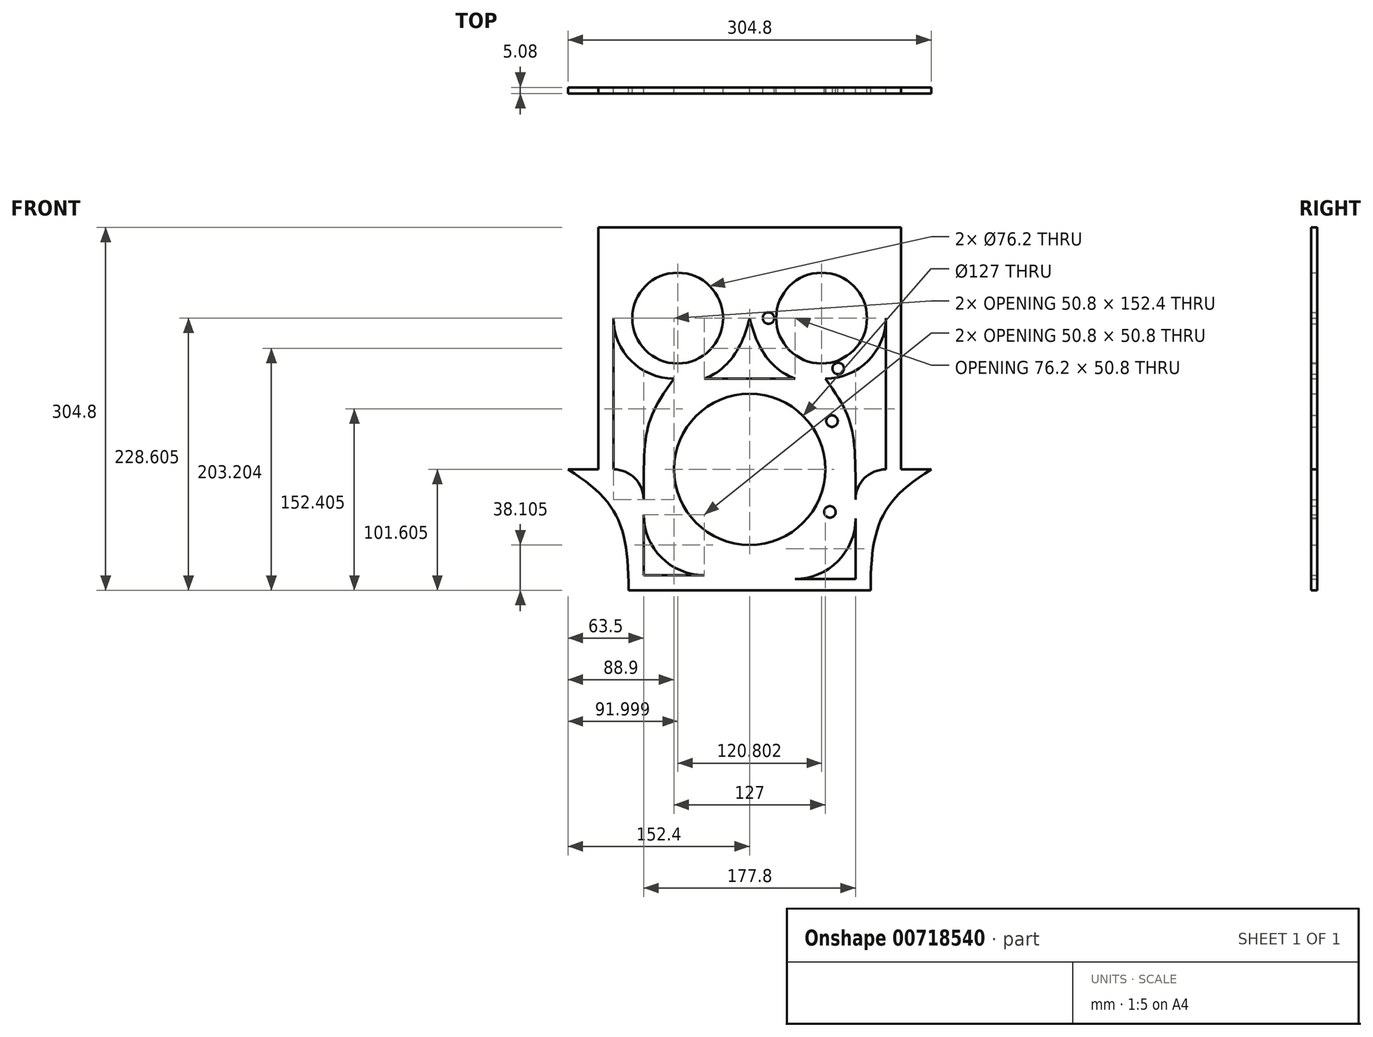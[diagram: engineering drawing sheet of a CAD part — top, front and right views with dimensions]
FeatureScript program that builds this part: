
annotation { "Feature Type Name" : "Feature", "Feature Type Description" : "" }
export const myFeature = defineFeature(function(context is Context, id is Id, definition is map)
    precondition{}
    {
        {
            var Q0;
            Q0=qCreatedBy(makeId("Front.planeOp"),FACE);
            var sketch = newSketch(context, id + "F0", { "sketchPlane" : qUnion([Q0])});
            skCircle(sketch, "E0", {"center": v(-60.4, 86.51) * mm, "radius": 38.1 * mm});
            skCircle(sketch, "E1", {"center": v(15.88, 86.51) * mm, "radius": 38.1 * mm, "construction": true});
            skCircle(sketch, "E2", {"center": v(15.88, 86.51) * mm, "radius": 6.35 * mm, "construction": true});
            skCircle(sketch, "E3", {"center": v(60.4, 86.51) * mm, "radius": 38.1 * mm});
            skLineSegment(sketch, "E4", {"start": v(-60.4, 86.51) * mm, "end": v(60.4, 86.51) * mm, "construction": true});
            skPoint(sketch, "E5", {"position": v(0, 86.51) * mm});
            skLineSegment(sketch, "E6", {"start": v(0, 86.51) * mm, "end": v(0, -40.49) * mm, "construction": true});
            skCircle(sketch, "E7", {"center": v(15.88, 86.51) * mm, "radius": 4.83 * mm});
            skCircle(sketch, "E8", {"center": v(-60.4, 86.51) * mm, "radius": 4.83 * mm});
            skCircle(sketch, "E9", {"center": v(60.4, 86.51) * mm, "radius": 4.83 * mm});
            skLineSegment(sketch, "E10", {"start": v(-60.4, 48.41) * mm, "end": v(-60.4, 23.01) * mm, "construction": true});
            skPoint(sketch, "E11", {"position": v(0, 23.01) * mm});
            skCircle(sketch, "E12", {"center": v(0, -40.49) * mm, "radius": 63.5 * mm});
            skCircle(sketch, "E13", {"center": v(0, -40.49) * mm, "radius": 4.83 * mm});
            skLineSegment(sketch, "E14", {"start": v(0, -40.49) * mm, "end": v(127, -40.49) * mm, "construction": true});
            skLineSegment(sketch, "E15", {"start": v(0, -40.49) * mm, "end": v(-127, -40.49) * mm, "construction": true});
            skLineSegment(sketch, "E16", {"start": v(-127, -40.49) * mm, "end": v(-152.4, -40.49) * mm});
            skLineSegment(sketch, "E17", {"start": v(127, -40.49) * mm, "end": v(152.4, -40.49) * mm});
            skLineSegment(sketch, "E18", {"start": v(0, -40.49) * mm, "end": v(0, -142.09) * mm});
            skLineSegment(sketch, "E19", {"start": v(0, -142.09) * mm, "end": v(101.6, -142.09) * mm});
            skLineSegment(sketch, "E20", {"start": v(0, -142.09) * mm, "end": v(-101.6, -142.09) * mm});
            skFitSpline(sketch, "E21", {"points": [v(152.4, -40.49) * mm, v(101.6, -142.09) * mm], "startDerivative": vector(-128.12, -79.75) * mm, "endDerivative": vector(0, -160.77) * mm});
            skFitSpline(sketch, "E22", {"points": [v(-152.4, -40.49) * mm, v(-101.6, -142.09) * mm], "startDerivative": vector(126.83, -79.75) * mm, "endDerivative": vector(0, -160.77) * mm});
            skPoint(sketch, "E23", {"position": v(-88.9, -142.09) * mm});
            skPoint(sketch, "E24", {"position": v(88.9, -142.09) * mm});
            skLineSegment(sketch, "E25", {"start": v(-88.9, -129.39) * mm, "end": v(-38.1, -129.39) * mm});
            skLineSegment(sketch, "E26", {"start": v(-88.9, -129.39) * mm, "end": v(-88.9, -78.59) * mm});
            skArc(sketch, "E27", {"start": v(-88.9, -78.59) * mm, "mid": v(-74.02, -114.5) * mm, "end": v(-38.1, -129.39) * mm});
            skLineSegment(sketch, "E28", {"start": v(88.9, -132.58) * mm, "end": v(38.1, -132.58) * mm});
            skLineSegment(sketch, "E29", {"start": v(88.9, -132.58) * mm, "end": v(88.9, -81.78) * mm});
            skArc(sketch, "E30", {"start": v(88.9, -81.78) * mm, "mid": v(74.02, -117.7) * mm, "end": v(38.1, -132.58) * mm});
            skLineSegment(sketch, "E31", {"start": v(0, 86.51) * mm, "end": v(0, 162.71) * mm, "construction": true});
            skLineSegment(sketch, "E32", {"start": v(0, 162.71) * mm, "end": v(127, 162.71) * mm});
            skLineSegment(sketch, "E33", {"start": v(0, 162.71) * mm, "end": v(-127, 162.71) * mm});
            skLineSegment(sketch, "E34", {"start": v(127, 162.71) * mm, "end": v(127, -40.49) * mm});
            skLineSegment(sketch, "E35", {"start": v(-127, 162.71) * mm, "end": v(-127, -40.49) * mm});
            skPoint(sketch, "E36", {"position": v(0, 48.41) * mm});
            skPoint(sketch, "E37", {"position": v(0, 35.71) * mm});
            skLineSegment(sketch, "E38", {"start": v(0, 35.71) * mm, "end": v(38.1, 35.71) * mm});
            skLineSegment(sketch, "E39", {"start": v(38.1, 35.71) * mm, "end": v(0, 35.71) * mm});
            skLineSegment(sketch, "E40", {"start": v(-38.1, 35.71) * mm, "end": v(0, 35.71) * mm});
            skFitSpline(sketch, "E41", {"points": [v(38.1, 35.71) * mm, v(0, 86.51) * mm], "startDerivative": vector(-65.4, 24.37) * mm, "endDerivative": vector(-17.13, 70.35) * mm});
            skFitSpline(sketch, "E42", {"points": [v(0, 86.51) * mm, v(-38.1, 35.71) * mm], "startDerivative": vector(-17.13, -70.35) * mm, "endDerivative": vector(-65.4, -24.37) * mm});
            skLineSegment(sketch, "E43", {"start": v(-114.3, 35.71) * mm, "end": v(-114.3, -40.49) * mm});
            skLineSegment(sketch, "E44", {"start": v(-114.3, 35.71) * mm, "end": v(-63.5, 35.71) * mm, "construction": true});
            skLineSegment(sketch, "E45", {"start": v(-114.3, 35.71) * mm, "end": v(-114.3, 86.51) * mm});
            skArc(sketch, "E46", {"start": v(-114.3, 86.51) * mm, "mid": v(-99.42, 50.6) * mm, "end": v(-63.5, 35.71) * mm});
            skPoint(sketch, "E47", {"position": v(-88.9, -40.49) * mm});
            skLineSegment(sketch, "E48", {"start": v(-88.9, -40.49) * mm, "end": v(-88.9, -65.89) * mm, "construction": true});
            skArc(sketch, "E49", {"start": v(-114.3, -40.49) * mm, "mid": v(-96.34, -47.92) * mm, "end": v(-88.9, -65.89) * mm});
            skFitSpline(sketch, "E50", {"points": [v(-63.5, 35.71) * mm, v(-88.9, -65.89) * mm], "startDerivative": vector(-76.2, -107.14) * mm, "endDerivative": vector(0, -173.8) * mm});
            skPoint(sketch, "E51", {"position": v(114.3, 35.71) * mm});
            skPoint(sketch, "E51.positionSnap0", {"position": v(-88.9, 35.71) * mm});
            skLineSegment(sketch, "E52", {"start": v(114.3, 35.71) * mm, "end": v(63.5, 35.71) * mm, "construction": true});
            skLineSegment(sketch, "E53", {"start": v(114.3, 35.71) * mm, "end": v(114.3, 86.51) * mm});
            skArc(sketch, "E54", {"start": v(114.3, 86.51) * mm, "mid": v(99.42, 50.6) * mm, "end": v(63.5, 35.71) * mm});
            skLineSegment(sketch, "E55", {"start": v(114.3, 35.71) * mm, "end": v(114.3, -40.49) * mm});
            skPoint(sketch, "E56", {"position": v(88.9, -65.89) * mm});
            skPoint(sketch, "E57", {"position": v(88.9, -40.49) * mm});
            skArc(sketch, "E58", {"start": v(114.3, -40.49) * mm, "mid": v(96.34, -47.92) * mm, "end": v(88.9, -65.89) * mm});
            skFitSpline(sketch, "E59", {"points": [v(63.5, 35.71) * mm, v(88.9, -65.89) * mm], "startDerivative": vector(76.2, -107.14) * mm, "endDerivative": vector(0, -173.8) * mm});
            skCircle(sketch, "E60", {"center": v(0, -40.49) * mm, "radius": 38.1 * mm, "construction": true});
            skCircle(sketch, "E61", {"center": v(67.37, -76.26) * mm, "radius": 38.1 * mm, "construction": true});
            skCircle(sketch, "E62", {"center": v(74.33, 44.22) * mm, "radius": 6.35 * mm, "construction": true});
            skPoint(sketch, "E63", {"position": v(114.3, -2.39) * mm});
            skCircle(sketch, "E64", {"center": v(69.13, 0) * mm, "radius": 38.1 * mm, "construction": true});
            skCircle(sketch, "E65", {"center": v(74.33, 44.22) * mm, "radius": 4.83 * mm});
            skCircle(sketch, "E66", {"center": v(69.13, 0) * mm, "radius": 4.83 * mm});
            skCircle(sketch, "E67", {"center": v(67.37, -76.26) * mm, "radius": 4.83 * mm});
            skSolve(sketch);
        }
        {
            var Q0;
            Q0 = qSketchRegion(id + "F0", true);
            extrude(context, id + "F1", {"entities" : qUnion([Q0]), "depth" : 5.08 * mm, "offsetDistance" : 25.4 * mm});
        }
    });
